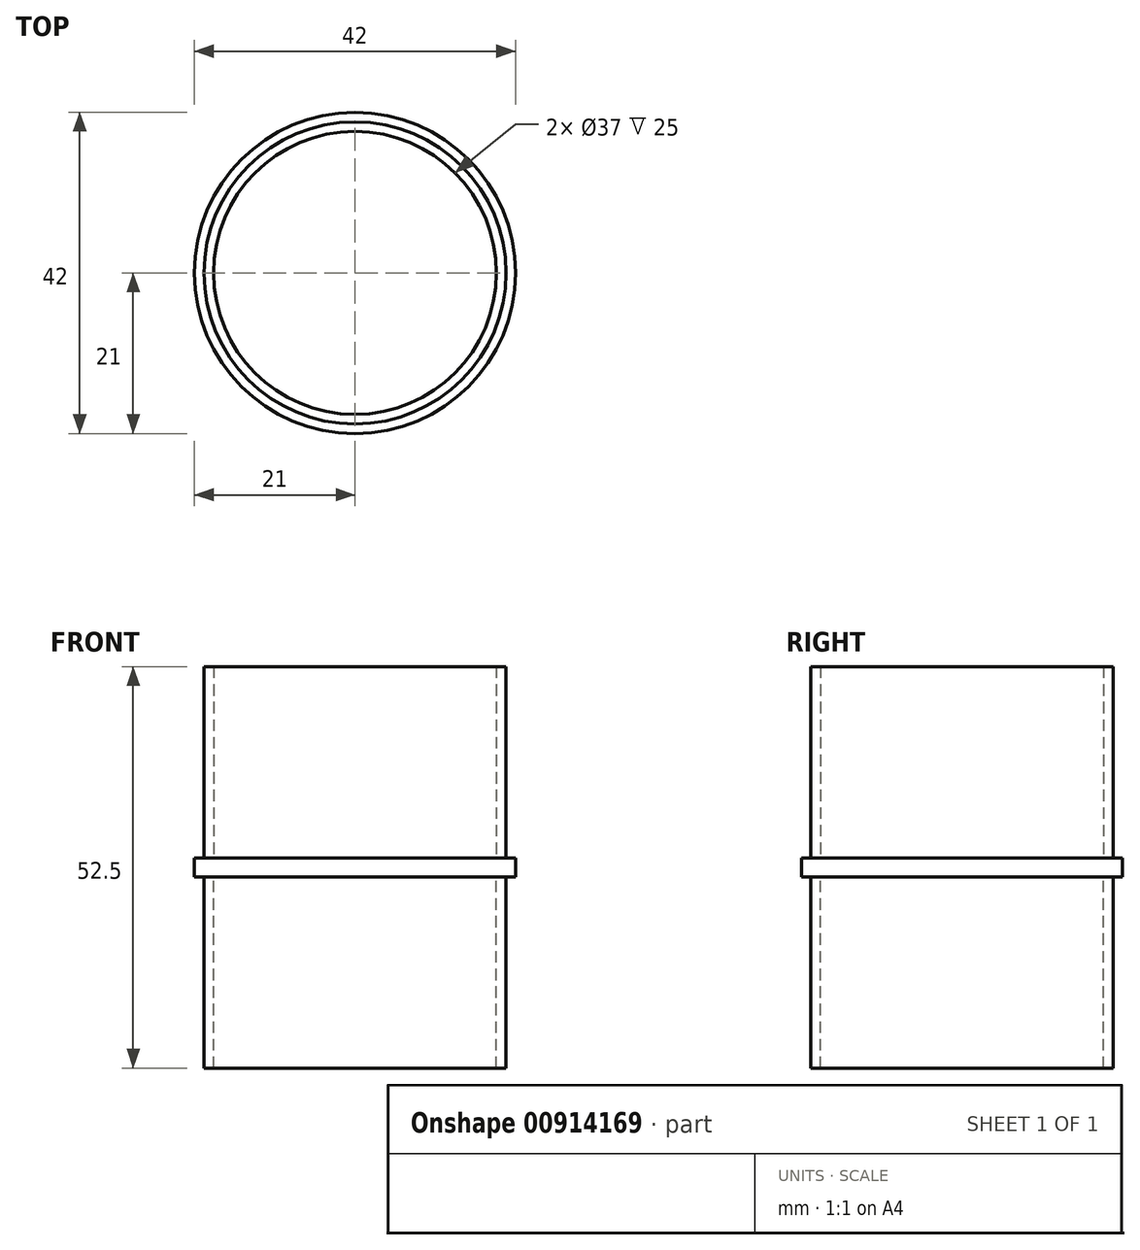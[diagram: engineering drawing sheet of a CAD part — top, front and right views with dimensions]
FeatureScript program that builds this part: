
annotation { "Feature Type Name" : "Feature", "Feature Type Description" : "" }
export const myFeature = defineFeature(function(context is Context, id is Id, definition is map)
    precondition{}
    {
        {
            var Q0;
            Q0=qCreatedBy(makeId("Top.planeOp"),FACE);
            var sketch = newSketch(context, id + "F0", { "sketchPlane" : qUnion([Q0])});
            skCircle(sketch, "E0", {"center": v(0, 0) * mm, "radius": 21 * mm});
            skSolve(sketch);
        }
        {
            var Q0;
            Q0=makeQuery(id+"F0.imprint","IMPRINT",FACE,{"disambiguationData":[TD([[makeQuery(id+"F0.imprint","IMPRINT",EDGE,{"derivedFrom":sQuery(id+"F0.wireOp",EDGE,"E0")}),1.0]])]});
            extrude(context, id + "F1", {"entities" : qUnion([Q0]), "depth" : 2.5 * mm, "offsetDistance" : 25 * mm});
        }
        {
            var Q0;
            Q0=makeQuery(id+"F1.opExtrude","CAP_FACE",FACE,{"disambiguationData":[OSD([sQuery(id+"F0.wireOp",EDGE,"E0")])],"isStart":false});
            var sketch = newSketch(context, id + "F2", { "sketchPlane" : qUnion([Q0])});
            skCircle(sketch, "E1", {"center": v(0, 0) * mm, "radius": 19.75 * mm});
            skSolve(sketch);
        }
        {
            var Q0;
            Q0=makeQuery(id+"F2.imprint","IMPRINT",FACE,{"disambiguationData":[TD([[makeQuery(id+"F2.imprint","IMPRINT",EDGE,{"derivedFrom":sQuery(id+"F2.wireOp",EDGE,"E1")}),1.0]])]});
            var sketch = newSketch(context, id + "F3", { "sketchPlane" : qUnion([Q0])});
            skCircle(sketch, "E2", {"center": v(0, 0) * mm, "radius": 18.5 * mm});
            skSolve(sketch);
        }
        {
            var Q0;
            Q0=makeQuery(id+"F3.imprint","IMPRINT",FACE,{"disambiguationData":[TD([[makeQuery(id+"F3.imprint","IMPRINT",EDGE,{"derivedFrom":sQuery(id+"F3.wireOp",EDGE,"E2")}),-1.0]])]});
            extrude(context, id + "F4", {"entities" : qUnion([Q0]), "operationType" : NewBodyOperationType.ADD, "depth" : 25 * mm, "offsetDistance" : 25 * mm});
        }
        {
            var Q0;
            Q0=makeQuery(id+"F1.opExtrude","CAP_FACE",FACE,{"disambiguationData":[OSD([sQuery(id+"F0.wireOp",EDGE,"E0")])],"isStart":true});
            var sketch = newSketch(context, id + "F5", { "sketchPlane" : qUnion([Q0])});
            skCircle(sketch, "E3", {"center": v(0, 0) * mm, "radius": 19.75 * mm});
            skSolve(sketch);
        }
        {
            var Q0;
            Q0=makeQuery(id+"F5.imprint","IMPRINT",FACE,{"disambiguationData":[TD([[makeQuery(id+"F5.imprint","IMPRINT",EDGE,{"derivedFrom":sQuery(id+"F5.wireOp",EDGE,"E3")}),1.0]])]});
            var sketch = newSketch(context, id + "F6", { "sketchPlane" : qUnion([Q0])});
            skCircle(sketch, "E4", {"center": v(0, 0) * mm, "radius": 18.5 * mm});
            skSolve(sketch);
        }
        {
            var Q0;
            Q0=makeQuery(id+"F6.imprint","IMPRINT",FACE,{"disambiguationData":[TD([[makeQuery(id+"F6.imprint","IMPRINT",EDGE,{"derivedFrom":sQuery(id+"F6.wireOp",EDGE,"E4")}),-1.0]])]});
            extrude(context, id + "F7", {"entities" : qUnion([Q0]), "operationType" : NewBodyOperationType.ADD, "depth" : 25 * mm, "offsetDistance" : 25 * mm});
        }
    });
